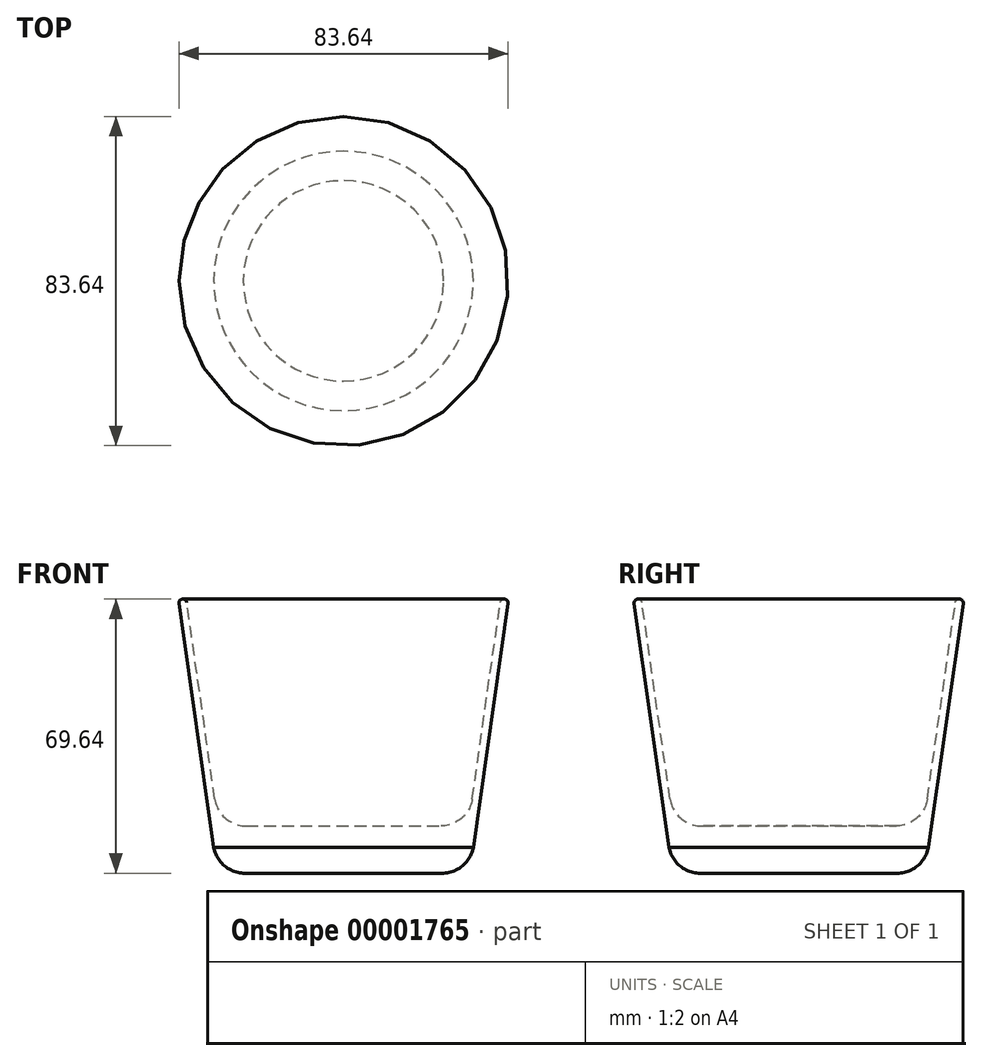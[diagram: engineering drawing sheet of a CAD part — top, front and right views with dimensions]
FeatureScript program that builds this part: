
annotation { "Feature Type Name" : "Feature", "Feature Type Description" : "" }
export const myFeature = defineFeature(function(context is Context, id is Id, definition is map)
    precondition{}
    {
        {
            var Q0;
            Q0=qCreatedBy(makeId("Front.planeOp"),FACE);
            var sketch = newSketch(context, id + "F0", { "sketchPlane" : qUnion([Q0])});
            skLineSegment(sketch, "E0", {"start": v(0, 0) * mm, "end": v(0, 70) * mm, "construction": true});
            skLineSegment(sketch, "E1", {"start": v(32.7, 18.87) * mm, "end": v(39.83, 68.79) * mm});
            skPoint(sketch, "E2.visualSharp", {"position": v(30, 0) * mm});
            skLineSegment(sketch, "E3.0", {"start": v(32.96, 6.59) * mm, "end": v(41.8, 68.5) * mm});
            skArc(sketch, "E3.1", {"start": v(25.46, 0) * mm, "mid": v(30.36, 1.98) * mm, "end": v(32.96, 6.59) * mm});
            skLineSegment(sketch, "E3.2", {"start": v(25.46, 0) * mm, "end": v(25.46, 0) * mm});
            skLineSegment(sketch, "E4.0", {"start": v(0, 12) * mm, "end": v(24.78, 12) * mm});
            skArc(sketch, "E5.filletArc", {"start": v(24.78, 12) * mm, "mid": v(30.02, 13.96) * mm, "end": v(32.7, 18.87) * mm});
            skPoint(sketch, "E6.orphan", {"position": v(40, 70) * mm});
            skArc(sketch, "E7", {"start": v(41.8, 68.5) * mm, "mid": v(40.96, 69.63) * mm, "end": v(39.83, 68.79) * mm});
            skLineSegment(sketch, "E8", {"start": v(0, 12) * mm, "end": v(0, 0) * mm});
            skLineSegment(sketch, "E9", {"start": v(0, 0) * mm, "end": v(25.46, 0) * mm});
            skSolve(sketch);
        }
        {
            var Q0;
            Q0 = qSketchRegion(id + "F0", true);
            var Q1;
            Q1=sQuery(id+"F0.wireOp",EDGE,"E0");
            revolve(context, id + "F1", {"entities" : qUnion([Q0]), "axis" : qUnion([Q1]), "revolveType" : RevolveType.FULL});
        }
    });
